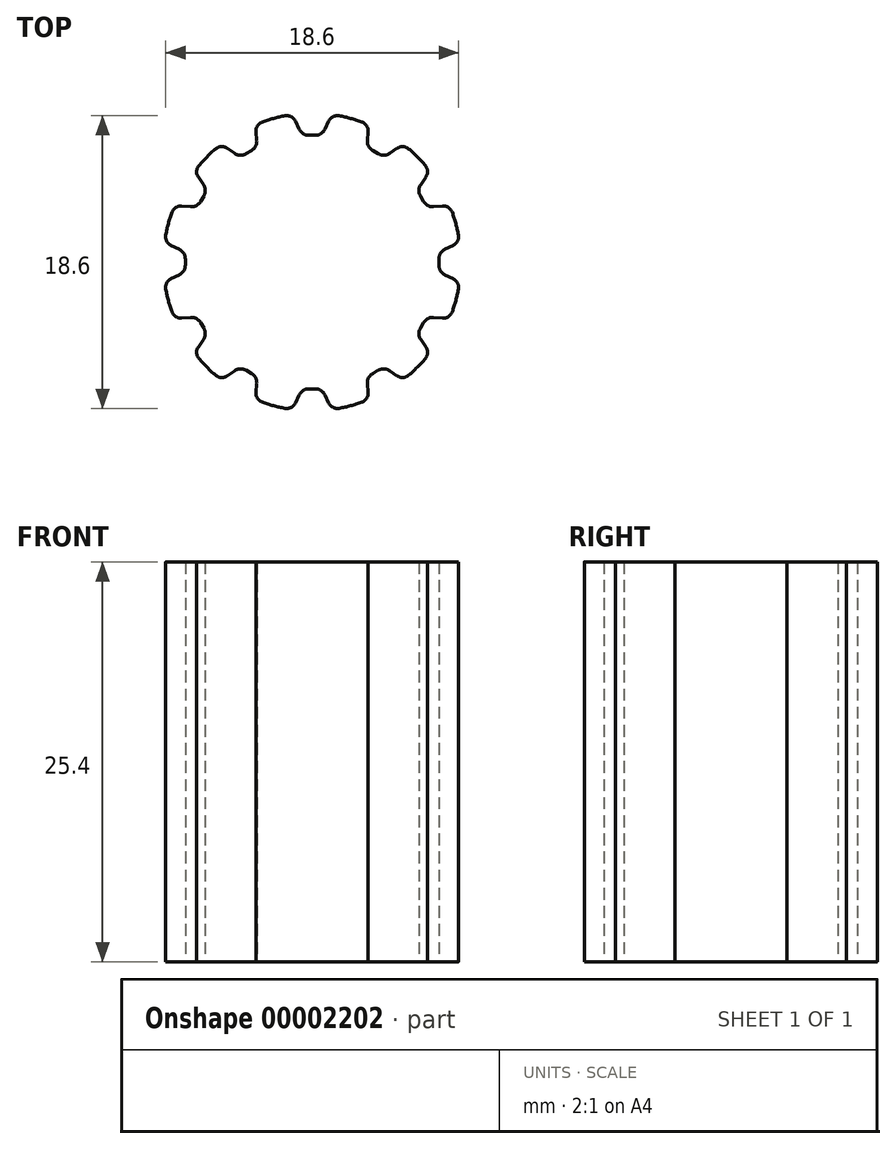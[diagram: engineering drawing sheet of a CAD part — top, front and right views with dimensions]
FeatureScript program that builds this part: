
annotation { "Feature Type Name" : "Feature", "Feature Type Description" : "" }
export const myFeature = defineFeature(function(context is Context, id is Id, definition is map)
    precondition{}
    {
        {
            var Q0;
            Q0=qCreatedBy(makeId("Top.planeOp"),FACE);
            var sketch = newSketch(context, id + "F0", { "sketchPlane" : qUnion([Q0])});
            skLineSegment(sketch, "E0.0.0", {"start": v(-0.82, 8.45) * mm, "end": v(-1.05, 8.95) * mm});
            skArc(sketch, "E0.0.1", {"start": v(-0.2, 8.05) * mm, "mid": v(-0.57, 8.16) * mm, "end": v(-0.82, 8.45) * mm});
            skLineSegment(sketch, "E0.0.2", {"start": v(0.2, 8.05) * mm, "end": v(-0.2, 8.05) * mm});
            skArc(sketch, "E0.0.3", {"start": v(0.82, 8.45) * mm, "mid": v(0.57, 8.16) * mm, "end": v(0.2, 8.05) * mm});
            skLineSegment(sketch, "E0.0.4", {"start": v(1.05, 8.95) * mm, "end": v(0.82, 8.45) * mm});
            skArc(sketch, "E0.0.5", {"start": v(1.05, 8.95) * mm, "mid": v(1.33, 9.23) * mm, "end": v(1.72, 9.3) * mm});
            skArc(sketch, "E0.0.6", {"start": v(1.72, 9.3) * mm, "mid": v(2.45, 9.13) * mm, "end": v(3.16, 8.9) * mm});
            skArc(sketch, "E0.0.7", {"start": v(3.16, 8.9) * mm, "mid": v(3.47, 8.66) * mm, "end": v(3.56, 8.28) * mm});
            skLineSegment(sketch, "E0.0.8", {"start": v(3.51, 7.73) * mm, "end": v(3.56, 8.28) * mm});
            skArc(sketch, "E0.0.9", {"start": v(3.85, 7.07) * mm, "mid": v(3.59, 7.35) * mm, "end": v(3.51, 7.73) * mm});
            skLineSegment(sketch, "E0.0.10", {"start": v(4.2, 6.87) * mm, "end": v(3.85, 7.07) * mm});
            skArc(sketch, "E0.0.11", {"start": v(4.93, 6.9) * mm, "mid": v(4.57, 6.78) * mm, "end": v(4.2, 6.87) * mm});
            skLineSegment(sketch, "E0.0.12", {"start": v(5.39, 7.22) * mm, "end": v(4.93, 6.9) * mm});
            skArc(sketch, "E0.0.13", {"start": v(5.39, 7.22) * mm, "mid": v(5.77, 7.33) * mm, "end": v(6.13, 7.19) * mm});
            skArc(sketch, "E0.0.14", {"start": v(6.13, 7.19) * mm, "mid": v(6.68, 6.68) * mm, "end": v(7.19, 6.13) * mm});
            skArc(sketch, "E0.0.15", {"start": v(7.19, 6.13) * mm, "mid": v(7.33, 5.77) * mm, "end": v(7.22, 5.39) * mm});
            skLineSegment(sketch, "E0.0.16", {"start": v(6.9, 4.93) * mm, "end": v(7.22, 5.39) * mm});
            skArc(sketch, "E0.0.17", {"start": v(6.87, 4.2) * mm, "mid": v(6.78, 4.57) * mm, "end": v(6.9, 4.93) * mm});
            skLineSegment(sketch, "E0.0.18", {"start": v(7.07, 3.85) * mm, "end": v(6.87, 4.2) * mm});
            skArc(sketch, "E0.0.19", {"start": v(7.73, 3.51) * mm, "mid": v(7.35, 3.59) * mm, "end": v(7.07, 3.85) * mm});
            skLineSegment(sketch, "E0.0.20", {"start": v(8.28, 3.56) * mm, "end": v(7.73, 3.51) * mm});
            skArc(sketch, "E0.0.21", {"start": v(8.28, 3.56) * mm, "mid": v(8.66, 3.47) * mm, "end": v(8.9, 3.16) * mm});
            skArc(sketch, "E0.0.22", {"start": v(8.9, 3.16) * mm, "mid": v(9.13, 2.45) * mm, "end": v(9.3, 1.72) * mm});
            skArc(sketch, "E0.0.23", {"start": v(9.3, 1.72) * mm, "mid": v(9.23, 1.33) * mm, "end": v(8.95, 1.05) * mm});
            skLineSegment(sketch, "E0.0.24", {"start": v(8.45, 0.82) * mm, "end": v(8.95, 1.05) * mm});
            skArc(sketch, "E0.0.25", {"start": v(8.05, 0.2) * mm, "mid": v(8.16, 0.57) * mm, "end": v(8.45, 0.82) * mm});
            skLineSegment(sketch, "E0.0.26", {"start": v(8.05, -0.2) * mm, "end": v(8.05, 0.2) * mm});
            skArc(sketch, "E0.0.27", {"start": v(8.45, -0.82) * mm, "mid": v(8.16, -0.57) * mm, "end": v(8.05, -0.2) * mm});
            skLineSegment(sketch, "E0.0.28", {"start": v(8.95, -1.05) * mm, "end": v(8.45, -0.82) * mm});
            skArc(sketch, "E0.0.29", {"start": v(8.95, -1.05) * mm, "mid": v(9.23, -1.33) * mm, "end": v(9.3, -1.72) * mm});
            skArc(sketch, "E0.0.30", {"start": v(9.3, -1.72) * mm, "mid": v(9.13, -2.45) * mm, "end": v(8.9, -3.16) * mm});
            skArc(sketch, "E0.0.31", {"start": v(8.9, -3.16) * mm, "mid": v(8.66, -3.47) * mm, "end": v(8.28, -3.56) * mm});
            skLineSegment(sketch, "E0.0.32", {"start": v(7.73, -3.51) * mm, "end": v(8.28, -3.56) * mm});
            skArc(sketch, "E0.0.33", {"start": v(7.07, -3.85) * mm, "mid": v(7.35, -3.59) * mm, "end": v(7.73, -3.51) * mm});
            skLineSegment(sketch, "E0.0.34", {"start": v(6.87, -4.2) * mm, "end": v(7.07, -3.85) * mm});
            skArc(sketch, "E0.0.35", {"start": v(6.9, -4.93) * mm, "mid": v(6.78, -4.57) * mm, "end": v(6.87, -4.2) * mm});
            skLineSegment(sketch, "E0.0.36", {"start": v(7.22, -5.39) * mm, "end": v(6.9, -4.93) * mm});
            skArc(sketch, "E0.0.37", {"start": v(7.22, -5.39) * mm, "mid": v(7.33, -5.77) * mm, "end": v(7.19, -6.13) * mm});
            skArc(sketch, "E0.0.38", {"start": v(7.19, -6.13) * mm, "mid": v(6.68, -6.68) * mm, "end": v(6.13, -7.19) * mm});
            skArc(sketch, "E0.0.39", {"start": v(6.13, -7.19) * mm, "mid": v(5.77, -7.33) * mm, "end": v(5.39, -7.22) * mm});
            skLineSegment(sketch, "E0.0.40", {"start": v(4.93, -6.9) * mm, "end": v(5.39, -7.22) * mm});
            skArc(sketch, "E0.0.41", {"start": v(4.2, -6.87) * mm, "mid": v(4.57, -6.78) * mm, "end": v(4.93, -6.9) * mm});
            skLineSegment(sketch, "E0.0.42", {"start": v(3.85, -7.07) * mm, "end": v(4.2, -6.87) * mm});
            skArc(sketch, "E0.0.43", {"start": v(3.51, -7.73) * mm, "mid": v(3.59, -7.35) * mm, "end": v(3.85, -7.07) * mm});
            skLineSegment(sketch, "E0.0.44", {"start": v(3.56, -8.28) * mm, "end": v(3.51, -7.73) * mm});
            skArc(sketch, "E0.0.45", {"start": v(3.56, -8.28) * mm, "mid": v(3.47, -8.66) * mm, "end": v(3.16, -8.9) * mm});
            skArc(sketch, "E0.0.46", {"start": v(3.16, -8.9) * mm, "mid": v(2.45, -9.13) * mm, "end": v(1.72, -9.3) * mm});
            skArc(sketch, "E0.0.47", {"start": v(1.72, -9.3) * mm, "mid": v(1.33, -9.23) * mm, "end": v(1.05, -8.95) * mm});
            skLineSegment(sketch, "E0.0.48", {"start": v(0.82, -8.45) * mm, "end": v(1.05, -8.95) * mm});
            skArc(sketch, "E0.0.49", {"start": v(0.2, -8.05) * mm, "mid": v(0.57, -8.16) * mm, "end": v(0.82, -8.45) * mm});
            skLineSegment(sketch, "E0.0.50", {"start": v(-0.2, -8.05) * mm, "end": v(0.2, -8.05) * mm});
            skArc(sketch, "E0.0.51", {"start": v(-0.82, -8.45) * mm, "mid": v(-0.57, -8.16) * mm, "end": v(-0.2, -8.05) * mm});
            skLineSegment(sketch, "E0.0.52", {"start": v(-1.05, -8.95) * mm, "end": v(-0.82, -8.45) * mm});
            skArc(sketch, "E0.0.53", {"start": v(-1.05, -8.95) * mm, "mid": v(-1.33, -9.23) * mm, "end": v(-1.72, -9.3) * mm});
            skArc(sketch, "E0.0.54", {"start": v(-1.72, -9.3) * mm, "mid": v(-2.45, -9.13) * mm, "end": v(-3.16, -8.9) * mm});
            skArc(sketch, "E0.0.55", {"start": v(-3.16, -8.9) * mm, "mid": v(-3.47, -8.66) * mm, "end": v(-3.56, -8.28) * mm});
            skLineSegment(sketch, "E0.0.56", {"start": v(-3.51, -7.73) * mm, "end": v(-3.56, -8.28) * mm});
            skArc(sketch, "E0.0.57", {"start": v(-3.85, -7.07) * mm, "mid": v(-3.59, -7.35) * mm, "end": v(-3.51, -7.73) * mm});
            skLineSegment(sketch, "E0.0.58", {"start": v(-4.2, -6.87) * mm, "end": v(-3.85, -7.07) * mm});
            skArc(sketch, "E0.0.59", {"start": v(-4.93, -6.9) * mm, "mid": v(-4.57, -6.78) * mm, "end": v(-4.2, -6.87) * mm});
            skLineSegment(sketch, "E0.0.60", {"start": v(-5.39, -7.22) * mm, "end": v(-4.93, -6.9) * mm});
            skArc(sketch, "E0.0.61", {"start": v(-5.39, -7.22) * mm, "mid": v(-5.77, -7.33) * mm, "end": v(-6.13, -7.19) * mm});
            skArc(sketch, "E0.0.62", {"start": v(-6.13, -7.19) * mm, "mid": v(-6.68, -6.68) * mm, "end": v(-7.19, -6.13) * mm});
            skArc(sketch, "E0.0.63", {"start": v(-7.19, -6.13) * mm, "mid": v(-7.33, -5.77) * mm, "end": v(-7.22, -5.39) * mm});
            skLineSegment(sketch, "E0.0.64", {"start": v(-6.9, -4.93) * mm, "end": v(-7.22, -5.39) * mm});
            skArc(sketch, "E0.0.65", {"start": v(-6.87, -4.2) * mm, "mid": v(-6.78, -4.57) * mm, "end": v(-6.9, -4.93) * mm});
            skLineSegment(sketch, "E0.0.66", {"start": v(-7.07, -3.85) * mm, "end": v(-6.87, -4.2) * mm});
            skArc(sketch, "E0.0.67", {"start": v(-7.73, -3.51) * mm, "mid": v(-7.35, -3.59) * mm, "end": v(-7.07, -3.85) * mm});
            skLineSegment(sketch, "E0.0.68", {"start": v(-8.28, -3.56) * mm, "end": v(-7.73, -3.51) * mm});
            skArc(sketch, "E0.0.69", {"start": v(-8.28, -3.56) * mm, "mid": v(-8.66, -3.47) * mm, "end": v(-8.9, -3.16) * mm});
            skArc(sketch, "E0.0.70", {"start": v(-8.9, -3.16) * mm, "mid": v(-9.13, -2.45) * mm, "end": v(-9.3, -1.72) * mm});
            skArc(sketch, "E0.0.71", {"start": v(-9.3, -1.72) * mm, "mid": v(-9.23, -1.33) * mm, "end": v(-8.95, -1.05) * mm});
            skLineSegment(sketch, "E0.0.72", {"start": v(-8.45, -0.82) * mm, "end": v(-8.95, -1.05) * mm});
            skArc(sketch, "E0.0.73", {"start": v(-8.05, -0.2) * mm, "mid": v(-8.16, -0.57) * mm, "end": v(-8.45, -0.82) * mm});
            skLineSegment(sketch, "E0.0.74", {"start": v(-8.05, 0.2) * mm, "end": v(-8.05, -0.2) * mm});
            skArc(sketch, "E0.0.75", {"start": v(-8.45, 0.82) * mm, "mid": v(-8.16, 0.57) * mm, "end": v(-8.05, 0.2) * mm});
            skLineSegment(sketch, "E0.0.76", {"start": v(-8.95, 1.05) * mm, "end": v(-8.45, 0.82) * mm});
            skArc(sketch, "E0.0.77", {"start": v(-8.95, 1.05) * mm, "mid": v(-9.23, 1.33) * mm, "end": v(-9.3, 1.72) * mm});
            skArc(sketch, "E0.0.78", {"start": v(-9.3, 1.72) * mm, "mid": v(-9.13, 2.45) * mm, "end": v(-8.9, 3.16) * mm});
            skArc(sketch, "E0.0.79", {"start": v(-8.9, 3.16) * mm, "mid": v(-8.66, 3.47) * mm, "end": v(-8.28, 3.56) * mm});
            skLineSegment(sketch, "E0.0.80", {"start": v(-7.73, 3.51) * mm, "end": v(-8.28, 3.56) * mm});
            skArc(sketch, "E0.0.81", {"start": v(-7.07, 3.85) * mm, "mid": v(-7.35, 3.59) * mm, "end": v(-7.73, 3.51) * mm});
            skLineSegment(sketch, "E0.0.82", {"start": v(-6.87, 4.2) * mm, "end": v(-7.07, 3.85) * mm});
            skArc(sketch, "E0.0.83", {"start": v(-6.9, 4.93) * mm, "mid": v(-6.78, 4.57) * mm, "end": v(-6.87, 4.2) * mm});
            skLineSegment(sketch, "E0.0.84", {"start": v(-7.22, 5.39) * mm, "end": v(-6.9, 4.93) * mm});
            skArc(sketch, "E0.0.85", {"start": v(-7.22, 5.39) * mm, "mid": v(-7.33, 5.77) * mm, "end": v(-7.19, 6.13) * mm});
            skArc(sketch, "E0.0.86", {"start": v(-7.19, 6.13) * mm, "mid": v(-6.68, 6.68) * mm, "end": v(-6.13, 7.19) * mm});
            skArc(sketch, "E0.0.87", {"start": v(-6.13, 7.19) * mm, "mid": v(-5.77, 7.33) * mm, "end": v(-5.39, 7.22) * mm});
            skLineSegment(sketch, "E0.0.88", {"start": v(-4.93, 6.9) * mm, "end": v(-5.39, 7.22) * mm});
            skArc(sketch, "E0.0.89", {"start": v(-4.2, 6.87) * mm, "mid": v(-4.57, 6.78) * mm, "end": v(-4.93, 6.9) * mm});
            skLineSegment(sketch, "E0.0.90", {"start": v(-3.85, 7.07) * mm, "end": v(-4.2, 6.87) * mm});
            skArc(sketch, "E0.0.91", {"start": v(-3.51, 7.73) * mm, "mid": v(-3.59, 7.35) * mm, "end": v(-3.85, 7.07) * mm});
            skLineSegment(sketch, "E0.0.92", {"start": v(-3.56, 8.28) * mm, "end": v(-3.51, 7.73) * mm});
            skArc(sketch, "E0.0.93", {"start": v(-3.56, 8.28) * mm, "mid": v(-3.47, 8.66) * mm, "end": v(-3.16, 8.9) * mm});
            skArc(sketch, "E0.0.94", {"start": v(-3.16, 8.9) * mm, "mid": v(-2.45, 9.13) * mm, "end": v(-1.72, 9.3) * mm});
            skArc(sketch, "E0.0.95", {"start": v(-1.72, 9.3) * mm, "mid": v(-1.33, 9.23) * mm, "end": v(-1.05, 8.95) * mm});
            skSolve(sketch);
        }
        {
            var Q0;
            Q0=makeQuery(id+"F0.imprint","IMPRINT",FACE,{"disambiguationData":[TD([[makeQuery(id+"F0.imprint","IMPRINT",EDGE,{"derivedFrom":sQuery(id+"F0.wireOp",EDGE,"E0.0.0")}),1.0]])]});
            extrude(context, id + "F1", {"entities" : qUnion([Q0]), "depth" : 25.4 * mm});
        }
    });
